# Revit family: NAU_Naughtone_Stng_Symbol_Curved1
name_source: partatom
category: Furniture
revit_build: Autodesk Revit 2018 (Build: 20170223_1515(x64)
units: mm (PartAtom-declared; Revit-internal decimal feet)

## family parameters
Always vertical = Yes
Cut with Voids When Loaded = No
OmniClass Number = 23.40.20.00
OmniClass Title = General Furniture and Specialties
Room Calculation Point = No
Shared = Yes
Work Plane-Based = No

## types (5) — shared parameters
Assembly Code = E2020200
AssetType = Moveable
BIMObjectName = Naughtone_Seating_Symbol_Curved
CodePerformance = PASSED BSEN 16139
Color = Various
DurationUnit = year
Finish = Upholstered
IfcExportAs = IfcFurnishingElementType
MainColor = Various
ManufacturerAddress = Knaresborough Tech Park, Manse Lane, Knaresborough, HG5 8LF
ManufacturerName = Naughtone
ManufacturerURL = www.naughtone.com
Material = Fabric, leather/steel/solid wood/beech ply/foam
NBSDescription = Seating
NBSReference = 45-35-72/352
Name = Seating_Symbol_Curved_Naughtone
ProductInformation = www.naughtone.com/portfolio-view/symbol
Shape = Curved
SustainabilityPerformance = FSC certified. FISP certified. ISO 14001 certified
Version = 2
WarrantyDescription = Request warranty information from naughtone
WarrantyDurationLabor = 7
WarrantyDurationParts = 7
WarrantyDurationUnit = year

## per-type parameters (varying)
| type | Category | Description | HasBack | IfcExportType | Is45 | Is45Bench | Is90 | IsBench | IsSYM45BEN | IsSYM45D | IsSYM90BEN | IsSYM90D | IsSYMX45D | Keynote | Model | ModelNumber | ModelReference | NominalHeight | NominalLength | NominalWidth | Size | URL | Uniclass2015Code | Uniclass2015Title |
| SYM90D - Symbol 90º Curve Sofa | Pr_40_50_12 : Chairs, seats and benches | Symbol 90º Degree Curve Seat | Yes | SOFA | No | No | Yes | No | No | No | No | Yes | No | Pr_40_50_12_07 | SYM90D | SYM90D | Symbol 90º Degree Curve Seat | 685 mm  [stored 2.24738 ft] | 1825 mm  [stored 5.98753 ft] | 865 mm  [stored 2.83793 ft] | 1825 x 865 x 685mm |  | Pr_40_50_12_07 | Benches |
| SYM90BEN - Symbol 90º Curve Bench | Pr_40_50_12_07 : Benches | Symbol 90º Degree Curve Bench | No | BENCH | No | No | Yes | Yes | No | No | Yes | No | No | Pr_40_50_12_07 | SYM90BEN | SYM90BEN | Symbol 90º Degree Curve Bench | 410 mm  [stored 1.34514 ft] | 1570 mm | 685 mm  [stored 2.24738 ft] | 1570 x 685 x 685mm | www.naughtone.com | Pr_40_50_12_07 | Benches |
| SYM45BEN - Symbol 45º Curve Bench | Pr_40_50_12_07 : Benches | Symbol 45º Curve Bench | No | BENCH | Yes | Yes | No | Yes | Yes | No | No | No | No | Pr_40_50_12_07 | SYM45BEN | SYM45BEN | Symbol 45º Curve Bench | 410 mm  [stored 1.34514 ft] | 1020 mm  [stored 3.34646 ft] | 510 mm  [stored 1.67323 ft] | 1020 x 510 x 410mm | www.naughtone.com | Pr_40_50_12_07 | Benches |
| SYM45D - Symbol 45º Curve Seat | Pr_40_50_12 : Chairs, seats and benches | Symbol 45º Curve Seat | Yes | SOFA | Yes | No | No | No | No | Yes | No | No | No | Pr_40_50_12 | SYM45D | SYM45D | Symbol 45º Curve Seat | 685 mm  [stored 2.24738 ft] | 1020 mm  [stored 3.34646 ft] | 690 mm  [stored 2.26378 ft] | 1020 x 690 x 685mm | www.naughtone.com | Pr_40_50_12 | Chairs, seats and benches |
| SYMX45D - Symbol External 45º Curve Sofa | Pr_40_50_12 : Chairs, seats and benches | Symbol External 45º Curve Sofa | Yes | SOFA | No | No | No | No | No | No | No | No | Yes | Pr_40_50_12 | SYMX45D | SYMX45D | Symbol External 45º Curve Sofa | 685 mm  [stored 2.24738 ft] | 1200 mm  [stored 3.93701 ft] | 690 mm  [stored 2.26378 ft] | 1200 x 690 x 685mm | www.naughtone.com | Pr_40_50_12 | Chairs, seats and benches |

note: [stored X ft] marks values corroborated as IEEE doubles in the binary element streams (Revit-internal decimal feet)

## geometry (parser evidence)
native form markers: Sweep x4
no freeform markers — native parametric forms only
